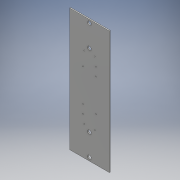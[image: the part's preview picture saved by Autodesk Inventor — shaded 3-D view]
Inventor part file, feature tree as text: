
AUTODESK INVENTOR PART (.ipt)
format: ipt  version: 2016 (Build 200138000, 138)  size: 172,032 bytes
history: native  units: mm
features: extrude x2, sketch x2, other x1
ambient origin geometry x8: Origin, YZ Plane, XZ Plane, XY Plane, X Axis, Y Axis, Z Axis, Center Point
bodies: Body1 (feature_tree)
feature tree (5):
  other  "ソリッド1"
  extrude  "押し出し1"  Depth=84.0mm
  extrude  "押し出し6"  Depth=260.0mm
  sketch  "スケッチ1"
  sketch  "スケッチ2"
